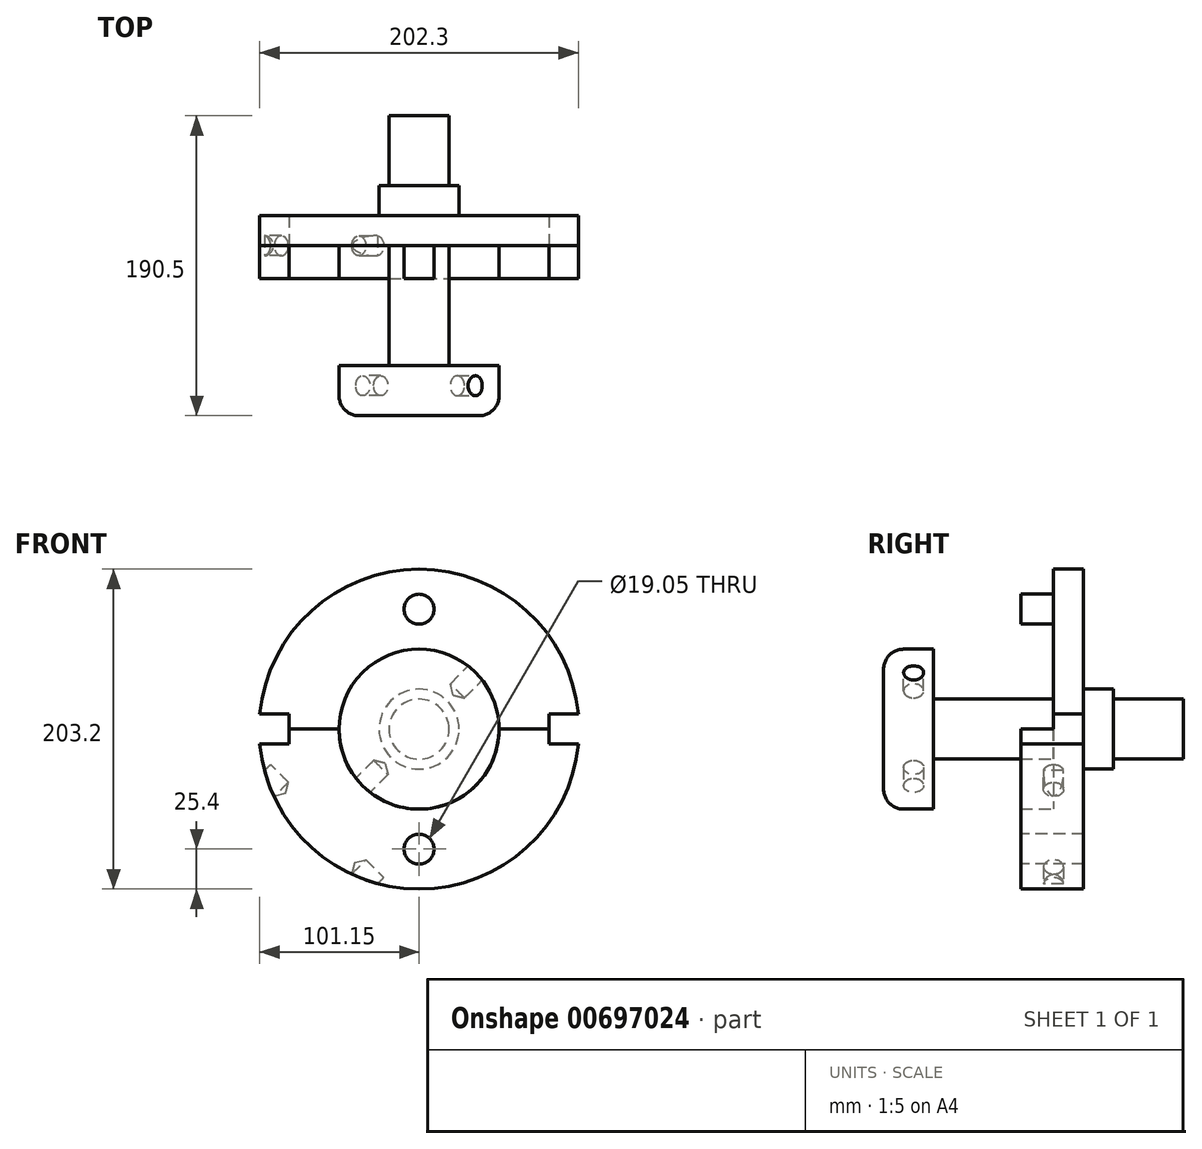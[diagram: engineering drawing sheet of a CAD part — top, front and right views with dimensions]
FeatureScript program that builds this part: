
annotation { "Feature Type Name" : "Feature", "Feature Type Description" : "" }
export const myFeature = defineFeature(function(context is Context, id is Id, definition is map)
    precondition{}
    {
        {
            var Q0;
            Q0=qCreatedBy(makeId("Front.planeOp"),FACE);
            var sketch = newSketch(context, id + "F0", { "sketchPlane" : qUnion([Q0])});
            skCircle(sketch, "E0", {"center": v(0, 0) * mm, "radius": 101.6 * mm});
            skCircle(sketch, "E1", {"center": v(0, 0) * mm, "radius": 76.2 * mm});
            skCircle(sketch, "E2", {"center": v(0, 0) * mm, "radius": 50.8 * mm});
            skCircle(sketch, "E3", {"center": v(0, 0) * mm, "radius": 19.05 * mm});
            skLineSegment(sketch, "E4", {"start": v(0, 0) * mm, "end": v(82.55, 0) * mm});
            skLineSegment(sketch, "E5", {"start": v(82.55, 0) * mm, "end": v(82.55, -9.53) * mm});
            skLineSegment(sketch, "E6", {"start": v(82.55, -9.53) * mm, "end": v(101.15, -9.53) * mm});
            skLineSegment(sketch, "E7", {"start": v(82.55, 0) * mm, "end": v(82.55, 9.53) * mm});
            skLineSegment(sketch, "E8", {"start": v(82.55, 9.53) * mm, "end": v(101.15, 9.53) * mm});
            skLineSegment(sketch, "E9", {"start": v(0, 0) * mm, "end": v(-82.55, 0) * mm});
            skLineSegment(sketch, "E10", {"start": v(-82.55, 0) * mm, "end": v(-82.55, -9.53) * mm});
            skLineSegment(sketch, "E11", {"start": v(-82.55, -9.53) * mm, "end": v(-101.15, -9.53) * mm});
            skLineSegment(sketch, "E12", {"start": v(-82.55, 0) * mm, "end": v(-82.55, 9.52) * mm});
            skLineSegment(sketch, "E13", {"start": v(-82.55, 9.52) * mm, "end": v(-101.15, 9.52) * mm});
            skCircle(sketch, "E14", {"center": v(0, 76.2) * mm, "radius": 9.53 * mm});
            skCircle(sketch, "E15", {"center": v(0, -76.2) * mm, "radius": 9.53 * mm});
            skCircle(sketch, "E16", {"center": v(0, 0) * mm, "radius": 25.4 * mm});
            skSolve(sketch);
        }
        {
            var Q0;
            {var subQ0=sQuery(id+"F0.wireOp",EDGE,"E7");Q0=makeQuery(id+"F0.imprint","IMPRINT",FACE,{"disambiguationData":[TD([[makeQuery(id+"F0.imprint","IMPRINT",EDGE,{"derivedFrom":subQ0}),1.0]])]});}
            var Q1;
            {var subQ5=sQuery(id+"F0.wireOp",EDGE,"E5");Q1=makeQuery(id+"F0.imprint","IMPRINT",FACE,{"disambiguationData":[TD([[makeQuery(id+"F0.imprint","IMPRINT",EDGE,{"derivedFrom":subQ5}),-1.0]])]});}
            var Q2;
            {var subQ1=sQuery(id+"F0.wireOp",EDGE,"E1");var subQ5=sQuery(id+"F0.wireOp",EDGE,"E9");var subQ9=makeQuery(id+"F0.imprint","INTERSECT",VERTEX,{"derivedFrom":[subQ1,subQ5]});Q2=makeQuery(id+"F0.imprint","IMPRINT",FACE,{"disambiguationData":[TD([[makeQuery(id+"F0.imprint","IMPRINT",EDGE,{"disambiguationData":[TD([[subQ9,-1.0]])],"derivedFrom":subQ1}),1.0]])]});}
            var Q3;
            {var subQ0=sQuery(id+"F0.wireOp",EDGE,"E4");var subQ1=sQuery(id+"F0.wireOp",EDGE,"E2");var subQ2=makeQuery(id+"F0.imprint","INTERSECT",VERTEX,{"derivedFrom":[subQ1,subQ0]});Q3=makeQuery(id+"F0.imprint","IMPRINT",FACE,{"disambiguationData":[TD([[makeQuery(id+"F0.imprint","IMPRINT",EDGE,{"disambiguationData":[TD([[subQ2,1.0]])],"derivedFrom":subQ1}),1.0]])]});}
            var Q4;
            {var subQ0=sQuery(id+"F0.wireOp",EDGE,"E4");var subQ1=sQuery(id+"F0.wireOp",EDGE,"E2");var subQ2=makeQuery(id+"F0.imprint","INTERSECT",VERTEX,{"derivedFrom":[subQ1,subQ0]});Q4=makeQuery(id+"F0.imprint","IMPRINT",FACE,{"disambiguationData":[TD([[makeQuery(id+"F0.imprint","IMPRINT",EDGE,{"disambiguationData":[TD([[subQ2,-1.0]])],"derivedFrom":subQ1}),1.0]])]});}
            var Q5;
            {var subQ5=sQuery(id+"F0.wireOp",EDGE,"E1");var subQ7=sQuery(id+"F0.wireOp",EDGE,"E14");var subQ10=makeQuery(id+"F0.imprint","INTERSECT",VERTEX,{"disambiguationData":[OD(0.0)],"derivedFrom":[subQ5,subQ7]});Q5=makeQuery(id+"F0.imprint","IMPRINT",FACE,{"disambiguationData":[TD([[makeQuery(id+"F0.imprint","IMPRINT",EDGE,{"disambiguationData":[TD([[subQ10,1.0]])],"derivedFrom":subQ5}),1.0]])]});}
            var Q6;
            {var subQ0=sQuery(id+"F0.wireOp",EDGE,"E4");var subQ1=sQuery(id+"F0.wireOp",EDGE,"E3");var subQ2=makeQuery(id+"F0.imprint","INTERSECT",VERTEX,{"derivedFrom":[subQ1,subQ0]});Q6=makeQuery(id+"F0.imprint","IMPRINT",FACE,{"disambiguationData":[TD([[makeQuery(id+"F0.imprint","IMPRINT",EDGE,{"disambiguationData":[TD([[subQ2,1.0]])],"derivedFrom":subQ1}),1.0]])]});}
            var Q7;
            {var subQ0=sQuery(id+"F0.wireOp",EDGE,"E4");var subQ1=sQuery(id+"F0.wireOp",EDGE,"E3");var subQ2=makeQuery(id+"F0.imprint","INTERSECT",VERTEX,{"derivedFrom":[subQ1,subQ0]});Q7=makeQuery(id+"F0.imprint","IMPRINT",FACE,{"disambiguationData":[TD([[makeQuery(id+"F0.imprint","IMPRINT",EDGE,{"disambiguationData":[TD([[subQ2,1.0]])],"derivedFrom":subQ1}),1.0]])]});}
            var Q8;
            {var subQ0=sQuery(id+"F0.wireOp",EDGE,"E4");var subQ1=sQuery(id+"F0.wireOp",EDGE,"E3");var subQ2=makeQuery(id+"F0.imprint","INTERSECT",VERTEX,{"derivedFrom":[subQ1,subQ0]});Q8=makeQuery(id+"F0.imprint","IMPRINT",FACE,{"disambiguationData":[TD([[makeQuery(id+"F0.imprint","IMPRINT",EDGE,{"disambiguationData":[TD([[subQ2,-1.0]])],"derivedFrom":subQ1}),1.0]])]});}
            var Q9;
            {var subQ0=sQuery(id+"F0.wireOp",EDGE,"E15");var subQ1=sQuery(id+"F0.wireOp",EDGE,"E1");var subQ2=makeQuery(id+"F0.imprint","INTERSECT",VERTEX,{"disambiguationData":[OD(0.0)],"derivedFrom":[subQ1,subQ0]});Q9=makeQuery(id+"F0.imprint","IMPRINT",FACE,{"disambiguationData":[TD([[makeQuery(id+"F0.imprint","IMPRINT",EDGE,{"disambiguationData":[TD([[subQ2,-1.0]])],"derivedFrom":subQ1}),-1.0]])]});}
            var Q10;
            {var subQ0=sQuery(id+"F0.wireOp",EDGE,"E14");var subQ1=sQuery(id+"F0.wireOp",EDGE,"E1");var subQ2=makeQuery(id+"F0.imprint","INTERSECT",VERTEX,{"disambiguationData":[OD(0.0)],"derivedFrom":[subQ1,subQ0]});Q10=makeQuery(id+"F0.imprint","IMPRINT",FACE,{"disambiguationData":[TD([[makeQuery(id+"F0.imprint","IMPRINT",EDGE,{"disambiguationData":[TD([[subQ2,-1.0]])],"derivedFrom":subQ1}),1.0]])]});}
            var Q11;
            {var subQ0=sQuery(id+"F0.wireOp",EDGE,"E14");var subQ1=sQuery(id+"F0.wireOp",EDGE,"E1");var subQ2=makeQuery(id+"F0.imprint","INTERSECT",VERTEX,{"disambiguationData":[OD(0.0)],"derivedFrom":[subQ1,subQ0]});Q11=makeQuery(id+"F0.imprint","IMPRINT",FACE,{"disambiguationData":[TD([[makeQuery(id+"F0.imprint","IMPRINT",EDGE,{"disambiguationData":[TD([[subQ2,-1.0]])],"derivedFrom":subQ1}),-1.0]])]});}
            var Q12;
            {var subQ0=sQuery(id+"F0.wireOp",EDGE,"E15");var subQ1=sQuery(id+"F0.wireOp",EDGE,"E1");var subQ2=makeQuery(id+"F0.imprint","INTERSECT",VERTEX,{"disambiguationData":[OD(0.0)],"derivedFrom":[subQ1,subQ0]});Q12=makeQuery(id+"F0.imprint","IMPRINT",FACE,{"disambiguationData":[TD([[makeQuery(id+"F0.imprint","IMPRINT",EDGE,{"disambiguationData":[TD([[subQ2,-1.0]])],"derivedFrom":subQ1}),1.0]])]});}
            var Q13;
            {var subQ0=sQuery(id+"F0.wireOp",EDGE,"E4");var subQ1=sQuery(id+"F0.wireOp",EDGE,"E3");var subQ2=makeQuery(id+"F0.imprint","INTERSECT",VERTEX,{"derivedFrom":[subQ1,subQ0]});Q13=makeQuery(id+"F0.imprint","IMPRINT",FACE,{"disambiguationData":[TD([[makeQuery(id+"F0.imprint","IMPRINT",EDGE,{"disambiguationData":[TD([[subQ2,1.0]])],"derivedFrom":subQ1}),-1.0]])]});}
            var Q14;
            {var subQ0=sQuery(id+"F0.wireOp",EDGE,"E4");var subQ1=sQuery(id+"F0.wireOp",EDGE,"E3");var subQ2=makeQuery(id+"F0.imprint","INTERSECT",VERTEX,{"derivedFrom":[subQ1,subQ0]});Q14=makeQuery(id+"F0.imprint","IMPRINT",FACE,{"disambiguationData":[TD([[makeQuery(id+"F0.imprint","IMPRINT",EDGE,{"disambiguationData":[TD([[subQ2,-1.0]])],"derivedFrom":subQ1}),-1.0]])]});}
            extrude(context, id + "F1", {"entities" : qUnion([Q0, Q1, Q2, Q3, Q4, Q5, Q6, Q7, Q8, Q9, Q10, Q11, Q12, Q13, Q14]), "oppositeDirection" : true, "depth" : 19.05 * mm});
        }
        {
            var Q0;
            {var subQ0=sQuery(id+"F0.wireOp",EDGE,"E4");var subQ1=sQuery(id+"F0.wireOp",EDGE,"E3");var subQ2=makeQuery(id+"F0.imprint","INTERSECT",VERTEX,{"derivedFrom":[subQ1,subQ0]});Q0=makeQuery(id+"F0.imprint","IMPRINT",FACE,{"disambiguationData":[TD([[makeQuery(id+"F0.imprint","IMPRINT",EDGE,{"disambiguationData":[TD([[subQ2,-1.0]])],"derivedFrom":subQ1}),1.0]])]});}
            var Q1;
            {var subQ0=sQuery(id+"F0.wireOp",EDGE,"E4");var subQ1=sQuery(id+"F0.wireOp",EDGE,"E3");var subQ2=makeQuery(id+"F0.imprint","INTERSECT",VERTEX,{"derivedFrom":[subQ1,subQ0]});Q1=makeQuery(id+"F0.imprint","IMPRINT",FACE,{"disambiguationData":[TD([[makeQuery(id+"F0.imprint","IMPRINT",EDGE,{"disambiguationData":[TD([[subQ2,1.0]])],"derivedFrom":subQ1}),1.0]])]});}
            extrude(context, id + "F2", {"entities" : qUnion([Q0, Q1]), "operationType" : NewBodyOperationType.ADD, "depth" : 76.2 * mm});
        }
        {
            var Q0;
            {var subQ0=sQuery(id+"F0.wireOp",EDGE,"E15");var subQ1=sQuery(id+"F0.wireOp",EDGE,"E1");var subQ2=makeQuery(id+"F0.imprint","INTERSECT",VERTEX,{"disambiguationData":[OD(0.0)],"derivedFrom":[subQ1,subQ0]});Q0=makeQuery(id+"F0.imprint","IMPRINT",FACE,{"disambiguationData":[TD([[makeQuery(id+"F0.imprint","IMPRINT",EDGE,{"disambiguationData":[TD([[subQ2,-1.0]])],"derivedFrom":subQ1}),1.0]])]});}
            var Q1;
            {var subQ0=sQuery(id+"F0.wireOp",EDGE,"E15");var subQ1=sQuery(id+"F0.wireOp",EDGE,"E1");var subQ2=makeQuery(id+"F0.imprint","INTERSECT",VERTEX,{"disambiguationData":[OD(0.0)],"derivedFrom":[subQ1,subQ0]});Q1=makeQuery(id+"F0.imprint","IMPRINT",FACE,{"disambiguationData":[TD([[makeQuery(id+"F0.imprint","IMPRINT",EDGE,{"disambiguationData":[TD([[subQ2,-1.0]])],"derivedFrom":subQ1}),-1.0]])]});}
            var Q2;
            {var subQ0=sQuery(id+"F0.wireOp",EDGE,"E14");var subQ1=sQuery(id+"F0.wireOp",EDGE,"E1");var subQ2=makeQuery(id+"F0.imprint","INTERSECT",VERTEX,{"disambiguationData":[OD(0.0)],"derivedFrom":[subQ1,subQ0]});Q2=makeQuery(id+"F0.imprint","IMPRINT",FACE,{"disambiguationData":[TD([[makeQuery(id+"F0.imprint","IMPRINT",EDGE,{"disambiguationData":[TD([[subQ2,-1.0]])],"derivedFrom":subQ1}),1.0]])]});}
            var Q3;
            {var subQ0=sQuery(id+"F0.wireOp",EDGE,"E14");var subQ1=sQuery(id+"F0.wireOp",EDGE,"E1");var subQ2=makeQuery(id+"F0.imprint","INTERSECT",VERTEX,{"disambiguationData":[OD(0.0)],"derivedFrom":[subQ1,subQ0]});Q3=makeQuery(id+"F0.imprint","IMPRINT",FACE,{"disambiguationData":[TD([[makeQuery(id+"F0.imprint","IMPRINT",EDGE,{"disambiguationData":[TD([[subQ2,-1.0]])],"derivedFrom":subQ1}),-1.0]])]});}
            extrude(context, id + "F3", {"entities" : qUnion([Q0, Q1, Q2, Q3]), "operationType" : NewBodyOperationType.ADD, "depth" : 20.83 * mm});
        }
        {
            var Q0;
            {var subQ0=sQuery(id+"F0.wireOp",EDGE,"E4");var subQ1=sQuery(id+"F0.wireOp",EDGE,"E3");var subQ2=makeQuery(id+"F0.imprint","INTERSECT",VERTEX,{"derivedFrom":[subQ1,subQ0]});Q0=makeQuery(id+"F0.imprint","IMPRINT",FACE,{"disambiguationData":[TD([[makeQuery(id+"F0.imprint","IMPRINT",EDGE,{"disambiguationData":[TD([[subQ2,-1.0]])],"derivedFrom":subQ1}),-1.0]])]});}
            var Q1;
            {var subQ0=sQuery(id+"F0.wireOp",EDGE,"E4");var subQ1=sQuery(id+"F0.wireOp",EDGE,"E3");var subQ2=makeQuery(id+"F0.imprint","INTERSECT",VERTEX,{"derivedFrom":[subQ1,subQ0]});Q1=makeQuery(id+"F0.imprint","IMPRINT",FACE,{"disambiguationData":[TD([[makeQuery(id+"F0.imprint","IMPRINT",EDGE,{"disambiguationData":[TD([[subQ2,1.0]])],"derivedFrom":subQ1}),-1.0]])]});}
            extrude(context, id + "F4", {"entities" : qUnion([Q0, Q1]), "operationType" : NewBodyOperationType.ADD, "oppositeDirection" : true, "depth" : 38.1 * mm});
        }
        {
            var Q0;
            Q0=makeQuery(id+"F4.boolean.opBoolean","SPLIT",FACE,{"disambiguationData":[TD([makeQuery(id+"F4.opExtrude","SWEPT_FACE",FACE,{"disambiguationData":[OSD([sQuery(id+"F0.wireOp",EDGE,"E3")])]})])],"derivedFrom":makeQuery(id+"F1.opExtrude","CAP_FACE",FACE,{"disambiguationData":[OSD([sQuery(id+"F0.wireOp",EDGE,"E0"),sQuery(id+"F0.wireOp",EDGE,"E5"),sQuery(id+"F0.wireOp",EDGE,"E6"),sQuery(id+"F0.wireOp",EDGE,"E7"),sQuery(id+"F0.wireOp",EDGE,"E8"),sQuery(id+"F0.wireOp",EDGE,"E10"),sQuery(id+"F0.wireOp",EDGE,"E11"),sQuery(id+"F0.wireOp",EDGE,"E12"),sQuery(id+"F0.wireOp",EDGE,"E13")])],"isStart":false})});
            extrude(context, id + "F5", {"entities" : qUnion([Q0]), "operationType" : NewBodyOperationType.ADD, "depth" : 63.5 * mm});
        }
        {
            var Q0;
            Q0=makeQuery(id+"F2.opExtrude","CAP_FACE",FACE,{"disambiguationData":[OSD([sQuery(id+"F0.wireOp",EDGE,"E3")])],"isStart":false});
            var sketch = newSketch(context, id + "F6", { "sketchPlane" : qUnion([Q0])});
            skCircle(sketch, "E17", {"center": v(0, 0) * mm, "radius": 50.8 * mm});
            skLineSegment(sketch, "E18.bottom", {"start": v(35.92, 35.92) * mm, "end": v(-35.92, 35.92) * mm, "construction": true});
            skLineSegment(sketch, "E18.top", {"start": v(35.92, -35.92) * mm, "end": v(-35.92, -35.92) * mm, "construction": true});
            skLineSegment(sketch, "E18.left", {"start": v(35.92, 35.92) * mm, "end": v(35.92, -35.92) * mm, "construction": true});
            skLineSegment(sketch, "E18.right", {"start": v(-35.92, 35.92) * mm, "end": v(-35.92, -35.92) * mm, "construction": true});
            skLineSegment(sketch, "E19", {"start": v(-35.92, 35.92) * mm, "end": v(35.92, -35.92) * mm, "construction": true});
            skLineSegment(sketch, "E20", {"start": v(35.92, 35.92) * mm, "end": v(-35.92, -35.92) * mm, "construction": true});
            skSolve(sketch);
        }
        {
            var Q0;
            Q0=makeQuery(id+"F6.imprint","IMPRINT",FACE,{"disambiguationData":[TD([[makeQuery(id+"F6.imprint","IMPRINT",EDGE,{"derivedFrom":sQuery(id+"F6.wireOp",EDGE,"E17")}),1.0]])]});
            var Q1;
            Q1=makeQuery(id+"F6.imprint","IMPRINT",FACE,{"disambiguationData":[TD([[makeQuery(id+"F6.imprint","IMPRINT",EDGE,{"derivedFrom":makeQuery(id+"F2.opExtrude","CAP_EDGE",EDGE,{"disambiguationData":[OSD([sQuery(id+"F0.wireOp",EDGE,"E3")])],"isStart":false})}),1.0]])]});
            extrude(context, id + "F7", {"entities" : qUnion([Q0, Q1]), "operationType" : NewBodyOperationType.ADD, "depth" : 31.75 * mm, "offsetDistance" : 25.4 * mm});
        }
        {
            var Q0;
            Q0=makeQuery(id+"F7.opExtrude","CAP_EDGE",EDGE,{"disambiguationData":[OSD([sQuery(id+"F6.wireOp",EDGE,"E17")])],"isStart":false});
            fillet(context, id + "F8", {"entities" : qUnion([Q0]), "radius" : 12.7 * mm, "tangentPropagation" : true, "allowEdgeOverflow" : false});
        }
        {
            var Q0;
            Q0=qCreatedBy(makeId("Right.planeOp"),FACE);
            var Q1;
            Q1=sQuery(id+"F6.wireOp",EDGE,"E19");
            cPlane(context, id + "F9", {"entities" : qUnion([Q0, Q1]), "cplaneType" : CPlaneType.LINE_ANGLE, "offset" : 25.4 * mm, "angle" : 0 * degree, "width" : 152.4 * mm, "height" : 152.4 * mm});
        }
        {
            var Q0;
            Q0=qCreatedBy(makeId("Right.planeOp"),FACE);
            var Q1;
            Q1=sQuery(id+"F6.wireOp",EDGE,"E20");
            cPlane(context, id + "F10", {"entities" : qUnion([Q0, Q1]), "cplaneType" : CPlaneType.LINE_ANGLE, "offset" : 25.4 * mm, "angle" : 0 * degree, "width" : 152.4 * mm, "height" : 152.4 * mm});
        }
        {
            var Q0;
            Q0=qCreatedBy(id+"F10.planeOp",FACE);
            cPlane(context, id + "F11", {"entities" : qUnion([Q0]), "cplaneType" : CPlaneType.OFFSET, "offset" : 50.8 * mm, "width" : 152.4 * mm, "height" : 152.4 * mm});
        }
        {
            var Q0;
            Q0=qCreatedBy(id+"F10.planeOp",FACE);
            cPlane(context, id + "F12", {"entities" : qUnion([Q0]), "cplaneType" : CPlaneType.OFFSET, "offset" : 50.8 * mm, "oppositeDirection" : true, "width" : 152.4 * mm, "height" : 152.4 * mm});
        }
        {
            var Q0;
            Q0=qCreatedBy(id+"F9.planeOp",FACE);
            cPlane(context, id + "F13", {"entities" : qUnion([Q0]), "cplaneType" : CPlaneType.OFFSET, "offset" : 50.8 * mm, "width" : 152.4 * mm, "height" : 152.4 * mm});
        }
        {
            var Q0;
            Q0=qCreatedBy(id+"F9.planeOp",FACE);
            cPlane(context, id + "F14", {"entities" : qUnion([Q0]), "cplaneType" : CPlaneType.OFFSET, "offset" : 50.8 * mm, "oppositeDirection" : true, "width" : 152.4 * mm, "height" : 152.4 * mm});
        }
        {
            var Q0;
            Q0=qCreatedBy(id+"F11.planeOp",FACE);
            var sketch = newSketch(context, id + "F15", { "sketchPlane" : qUnion([Q0])});
            skLineSegment(sketch, "E21.0", {"start": v(50.8, -76.2) * mm, "end": v(-50.8, -76.2) * mm});
            skLineSegment(sketch, "E22", {"start": v(38.1, -107.95) * mm, "end": v(-38.1, -107.95) * mm});
            skLineSegment(sketch, "E23", {"start": v(0, -76.2) * mm, "end": v(0, -88.9) * mm});
            skCircle(sketch, "E24", {"center": v(0, -88.9) * mm, "radius": 6.35 * mm});
            skSolve(sketch);
        }
        {
            var Q0;
            Q0=qCreatedBy(id+"F14.planeOp",FACE);
            var sketch = newSketch(context, id + "F16", { "sketchPlane" : qUnion([Q0])});
            skLineSegment(sketch, "E25.0", {"start": v(76.2, 50.8) * mm, "end": v(76.2, -50.8) * mm});
            skLineSegment(sketch, "E26", {"start": v(76.2, 0) * mm, "end": v(88.9, 0) * mm});
            skCircle(sketch, "E27", {"center": v(88.9, 0) * mm, "radius": 6.35 * mm});
            skSolve(sketch);
        }
        {
            var Q0;
            Q0=qCreatedBy(id+"F12.planeOp",FACE);
            var sketch = newSketch(context, id + "F17", { "sketchPlane" : qUnion([Q0])});
            skLineSegment(sketch, "E28.0", {"start": v(50.8, -76.2) * mm, "end": v(-50.8, -76.2) * mm});
            skLineSegment(sketch, "E29", {"start": v(0, -76.2) * mm, "end": v(0, -88.9) * mm});
            skCircle(sketch, "E30", {"center": v(0, -88.9) * mm, "radius": 6.35 * mm});
            skSolve(sketch);
        }
        {
            var Q0;
            Q0=qCreatedBy(id+"F13.planeOp",FACE);
            var sketch = newSketch(context, id + "F18", { "sketchPlane" : qUnion([Q0])});
            skLineSegment(sketch, "E31.0", {"start": v(76.2, 50.8) * mm, "end": v(76.2, -50.8) * mm});
            skLineSegment(sketch, "E32", {"start": v(76.2, 0) * mm, "end": v(88.9, 0) * mm});
            skCircle(sketch, "E33", {"center": v(88.9, 0) * mm, "radius": 6.35 * mm});
            skSolve(sketch);
        }
        {
            var Q0;
            Q0=sQuery(id+"F17.wireOp",VERTEX,"E30.center");
            var Q1;
            Q1=makeQuery(id+"F1.opExtrude","SWEPT_BODY",BODY,{"disambiguationData":[OSD([sQuery(id+"F0.wireOp",EDGE,"E0"),sQuery(id+"F0.wireOp",EDGE,"E5"),sQuery(id+"F0.wireOp",EDGE,"E6"),sQuery(id+"F0.wireOp",EDGE,"E7"),sQuery(id+"F0.wireOp",EDGE,"E8"),sQuery(id+"F0.wireOp",EDGE,"E10"),sQuery(id+"F0.wireOp",EDGE,"E11"),sQuery(id+"F0.wireOp",EDGE,"E12"),sQuery(id+"F0.wireOp",EDGE,"E13")])]});
            hole(context, id + "F19", {"style" : HoleStyle.SIMPLE, "endStyle" : HoleEndStyle.BLIND, "oppositeDirection" : true, "holeDiameter" : 12.7 * mm, "majorDiameter" : 6.35 * mm, "holeDepth" : 16 * mm, "isTappedThrough" : true, "tappedDepth" : 12.7 * mm, "tapClearance" : 3, "locations" : qUnion([Q0]), "scope" : qUnion([Q1])});
        }
        {
            var Q0;
            Q0=sQuery(id+"F18.wireOp",VERTEX,"E33.center");
            var Q1;
            Q1=makeQuery(id+"F1.opExtrude","SWEPT_BODY",BODY,{"disambiguationData":[OSD([sQuery(id+"F0.wireOp",EDGE,"E0"),sQuery(id+"F0.wireOp",EDGE,"E5"),sQuery(id+"F0.wireOp",EDGE,"E6"),sQuery(id+"F0.wireOp",EDGE,"E7"),sQuery(id+"F0.wireOp",EDGE,"E8"),sQuery(id+"F0.wireOp",EDGE,"E10"),sQuery(id+"F0.wireOp",EDGE,"E11"),sQuery(id+"F0.wireOp",EDGE,"E12"),sQuery(id+"F0.wireOp",EDGE,"E13")])]});
            hole(context, id + "F20", {"style" : HoleStyle.SIMPLE, "endStyle" : HoleEndStyle.BLIND, "holeDiameter" : 12.7 * mm, "majorDiameter" : 6.35 * mm, "holeDepth" : 16 * mm, "isTappedThrough" : true, "tappedDepth" : 12.7 * mm, "tapClearance" : 3, "locations" : qUnion([Q0]), "scope" : qUnion([Q1])});
        }
        {
            var Q0;
            Q0=sQuery(id+"F16.wireOp",VERTEX,"E27.center");
            var Q1;
            Q1=makeQuery(id+"F1.opExtrude","SWEPT_BODY",BODY,{"disambiguationData":[OSD([sQuery(id+"F0.wireOp",EDGE,"E0"),sQuery(id+"F0.wireOp",EDGE,"E5"),sQuery(id+"F0.wireOp",EDGE,"E6"),sQuery(id+"F0.wireOp",EDGE,"E7"),sQuery(id+"F0.wireOp",EDGE,"E8"),sQuery(id+"F0.wireOp",EDGE,"E10"),sQuery(id+"F0.wireOp",EDGE,"E11"),sQuery(id+"F0.wireOp",EDGE,"E12"),sQuery(id+"F0.wireOp",EDGE,"E13")])]});
            hole(context, id + "F21", {"style" : HoleStyle.SIMPLE, "endStyle" : HoleEndStyle.BLIND, "oppositeDirection" : true, "holeDiameter" : 12.7 * mm, "majorDiameter" : 6.35 * mm, "holeDepth" : 16 * mm, "isTappedThrough" : true, "tappedDepth" : 12.7 * mm, "tapClearance" : 3, "locations" : qUnion([Q0]), "scope" : qUnion([Q1])});
        }
        {
            var Q0;
            Q0=sQuery(id+"F15.wireOp",VERTEX,"E24.center");
            var Q1;
            Q1=makeQuery(id+"F1.opExtrude","SWEPT_BODY",BODY,{"disambiguationData":[OSD([sQuery(id+"F0.wireOp",EDGE,"E0"),sQuery(id+"F0.wireOp",EDGE,"E5"),sQuery(id+"F0.wireOp",EDGE,"E6"),sQuery(id+"F0.wireOp",EDGE,"E7"),sQuery(id+"F0.wireOp",EDGE,"E8"),sQuery(id+"F0.wireOp",EDGE,"E10"),sQuery(id+"F0.wireOp",EDGE,"E11"),sQuery(id+"F0.wireOp",EDGE,"E12"),sQuery(id+"F0.wireOp",EDGE,"E13")])]});
            hole(context, id + "F22", {"style" : HoleStyle.SIMPLE, "endStyle" : HoleEndStyle.BLIND, "holeDiameter" : 12.7 * mm, "majorDiameter" : 6.35 * mm, "holeDepth" : 16 * mm, "isTappedThrough" : true, "tappedDepth" : 12.7 * mm, "tapClearance" : 3, "locations" : qUnion([Q0]), "scope" : qUnion([Q1])});
        }
    });
